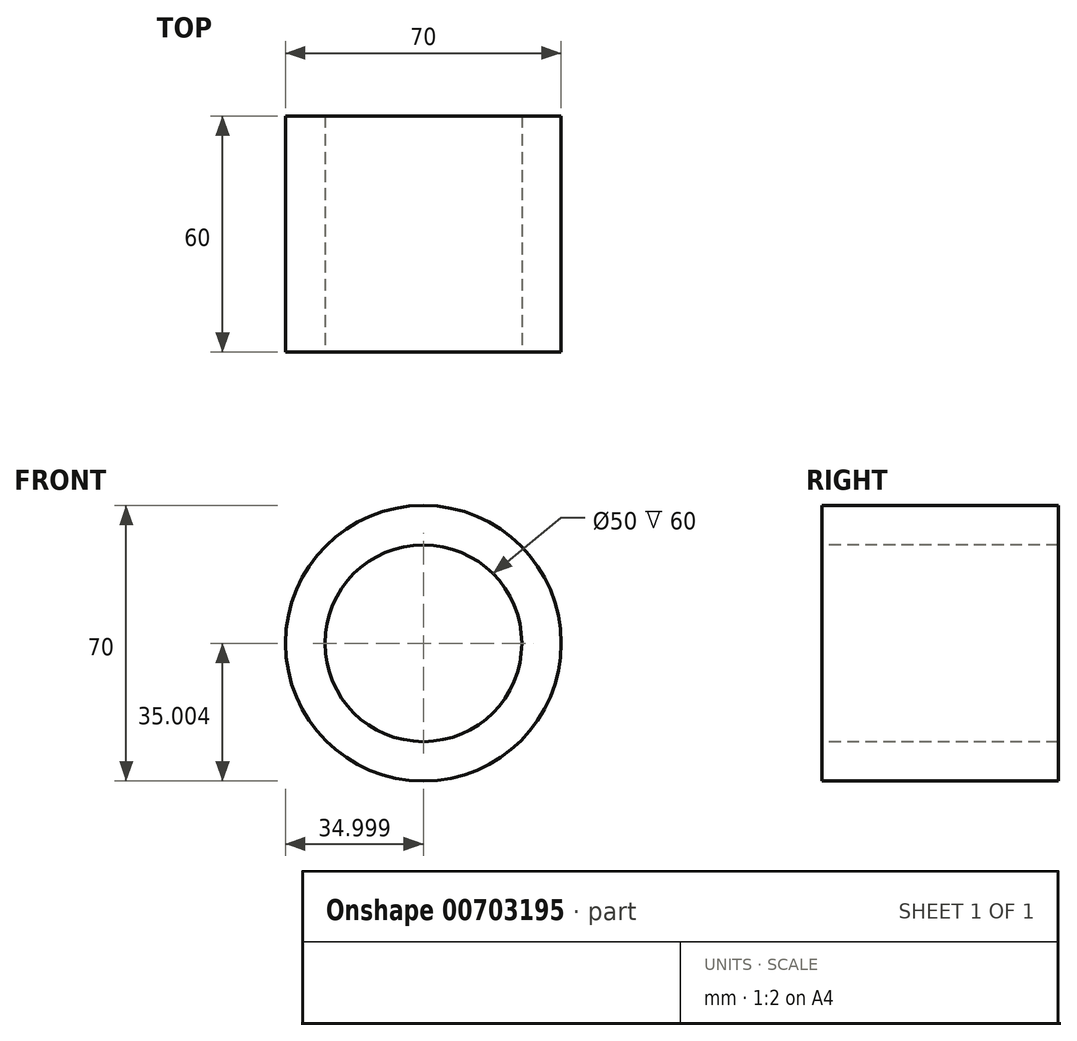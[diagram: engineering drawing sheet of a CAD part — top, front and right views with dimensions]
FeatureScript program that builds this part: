
annotation { "Feature Type Name" : "Feature", "Feature Type Description" : "" }
export const myFeature = defineFeature(function(context is Context, id is Id, definition is map)
    precondition{}
    {
        {
            var Q0;
            Q0=qCreatedBy(makeId("Front.planeOp"),FACE);
            var sketch = newSketch(context, id + "F0", { "sketchPlane" : qUnion([Q0])});
            skCircle(sketch, "E0", {"center": v(-41.6, 30.94) * mm, "radius": 35 * mm});
            skCircle(sketch, "E1", {"center": v(-41.6, 30.94) * mm, "radius": 25 * mm});
            skSolve(sketch);
        }
        {
            var Q0;
            Q0=makeQuery(id+"F0.imprint","IMPRINT",FACE,{"disambiguationData":[TD([[makeQuery(id+"F0.imprint","IMPRINT",EDGE,{"derivedFrom":sQuery(id+"F0.wireOp",EDGE,"E0")}),1.0]])]});
            extrude(context, id + "F1", {"entities" : qUnion([Q0]), "oppositeDirection" : true, "depth" : 60 * mm, "offsetDistance" : 25 * mm});
        }
        {
            var Q0;
            Q0 = qSketchRegion(id + "F0", true);
            extrude(context, id + "F2", {"entities" : qUnion([Q0]), "operationType" : NewBodyOperationType.ADD, "oppositeDirection" : true, "depth" : 25 * mm, "offsetDistance" : 25 * mm});
        }
    });
